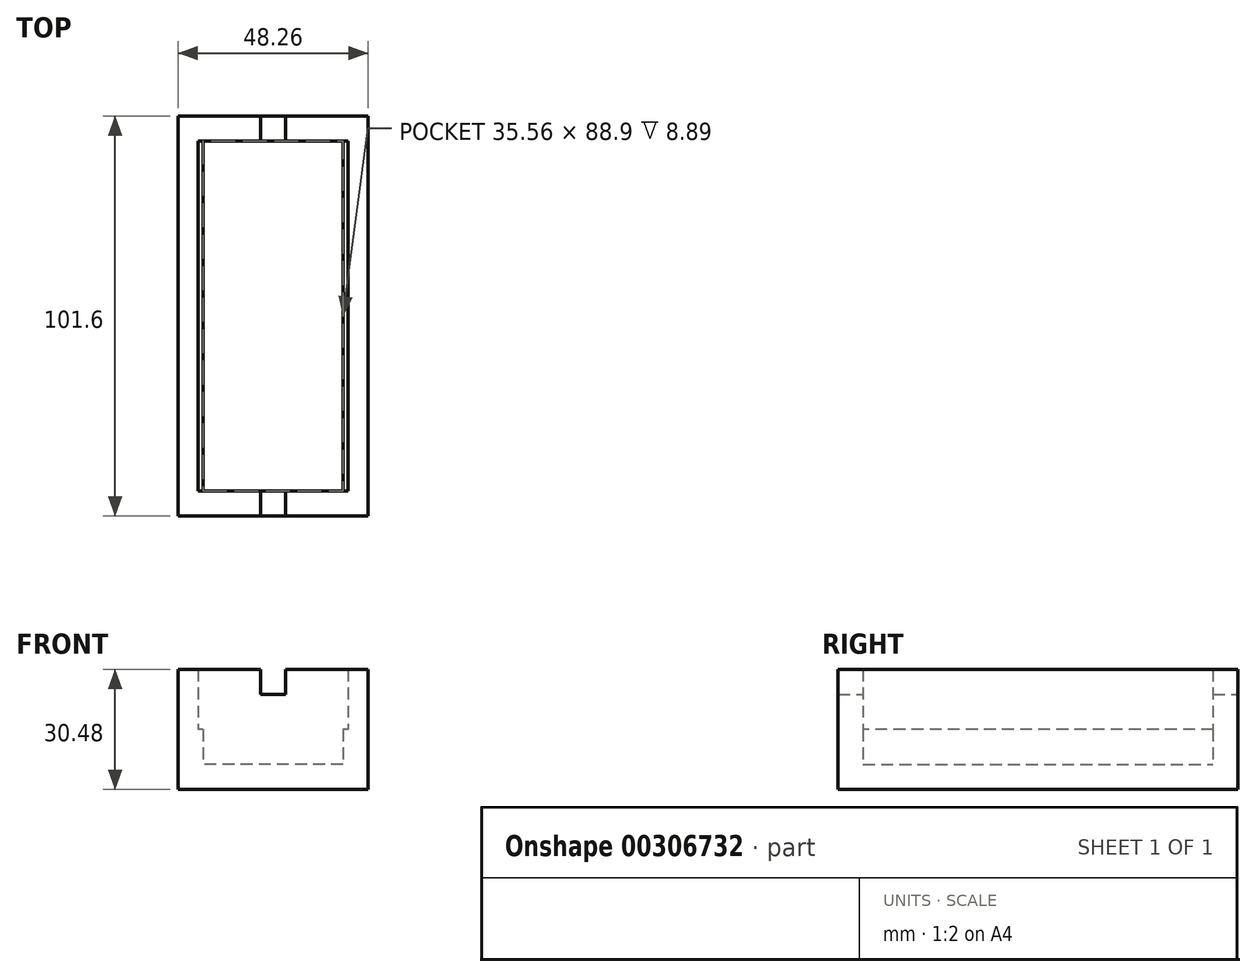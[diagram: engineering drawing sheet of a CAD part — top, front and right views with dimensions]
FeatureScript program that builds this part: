
annotation { "Feature Type Name" : "Feature", "Feature Type Description" : "" }
export const myFeature = defineFeature(function(context is Context, id is Id, definition is map)
    precondition{}
    {
        {
            var Q0;
            Q0=qCreatedBy(makeId("Front.planeOp"),FACE);
            var sketch = newSketch(context, id + "F0", { "sketchPlane" : qUnion([Q0])});
            skLineSegment(sketch, "E0.bottom", {"start": v(24.13, 15.24) * mm, "end": v(-24.13, 15.24) * mm});
            skLineSegment(sketch, "E0.top", {"start": v(24.13, -15.24) * mm, "end": v(-24.13, -15.24) * mm});
            skLineSegment(sketch, "E0.left", {"start": v(24.13, 15.24) * mm, "end": v(24.13, -15.24) * mm});
            skLineSegment(sketch, "E0.right", {"start": v(-24.13, 15.24) * mm, "end": v(-24.13, -15.24) * mm});
            skPoint(sketch, "E0.middle", {"position": v(0, 0) * mm});
            skLineSegment(sketch, "E1.bottom", {"start": v(-19.05, 15.24) * mm, "end": v(19.05, 15.24) * mm});
            skLineSegment(sketch, "E1.top", {"start": v(-19.05, -10.16) * mm, "end": v(19.05, -10.16) * mm});
            skLineSegment(sketch, "E1.left", {"start": v(-19.05, 15.24) * mm, "end": v(-19.05, -10.16) * mm});
            skLineSegment(sketch, "E1.right", {"start": v(19.05, 15.24) * mm, "end": v(19.05, -10.16) * mm});
            skLineSegment(sketch, "E2.bottom", {"start": v(-3.17, 15.24) * mm, "end": v(3.18, 15.24) * mm});
            skLineSegment(sketch, "E3.top", {"start": v(-3.17, 8.87) * mm, "end": v(3.18, 8.87) * mm});
            skLineSegment(sketch, "E3.left", {"start": v(-3.17, 15.24) * mm, "end": v(-3.17, 8.87) * mm});
            skLineSegment(sketch, "E3.right", {"start": v(3.18, 15.24) * mm, "end": v(3.18, 8.87) * mm});
            skSolve(sketch);
        }
        {
            var Q0;
            Q0=makeQuery(id+"F0.imprint","IMPRINT",FACE,{"disambiguationData":[TD([[makeQuery(id+"F0.imprint","IMPRINT",EDGE,{"derivedFrom":sQuery(id+"F0.wireOp",EDGE,"E0.top")}),-1.0]])]});
            extrude(context, id + "F1", {"entities" : qUnion([Q0]), "depth" : 50.8 * mm});
        }
        {
            var Q0;
            Q0=makeQuery(id+"F0.imprint","IMPRINT",FACE,{"disambiguationData":[TD([[makeQuery(id+"F0.imprint","IMPRINT",EDGE,{"derivedFrom":sQuery(id+"F0.wireOp",EDGE,"E1.top")}),1.0]])]});
            extrude(context, id + "F2", {"entities" : qUnion([Q0]), "operationType" : NewBodyOperationType.ADD, "depth" : 50.8 * mm});
        }
        {
            var Q0;
            Q0=makeQuery(id+"F1.opExtrude","SWEPT_BODY",BODY,{"disambiguationData":[OSD([sQuery(id+"F0.wireOp",EDGE,"E0.bottom"),sQuery(id+"F0.wireOp",EDGE,"E0.top"),sQuery(id+"F0.wireOp",EDGE,"E0.left"),sQuery(id+"F0.wireOp",EDGE,"E0.right"),sQuery(id+"F0.wireOp",EDGE,"E1.top"),sQuery(id+"F0.wireOp",EDGE,"E1.left"),sQuery(id+"F0.wireOp",EDGE,"E1.right")])]});
            var Q1;
            Q1=qCreatedBy(makeId("Front.planeOp"),FACE);
            mirror(context, id + "F3", {"operationType" : NewBodyOperationType.ADD, "entities" : qUnion([Q0]), "mirrorPlane" : qUnion([Q1])});
        }
        {
            var Q0;
            Q0=qCreatedBy(makeId("Top.planeOp"),FACE);
            var sketch = newSketch(context, id + "F4", { "sketchPlane" : qUnion([Q0])});
            skLineSegment(sketch, "E4.bottom", {"start": v(19.05, 44.45) * mm, "end": v(-19.05, 44.45) * mm});
            skLineSegment(sketch, "E4.top", {"start": v(19.05, -44.45) * mm, "end": v(-19.05, -44.45) * mm});
            skLineSegment(sketch, "E4.left", {"start": v(19.05, 44.45) * mm, "end": v(19.05, -44.45) * mm});
            skLineSegment(sketch, "E4.right", {"start": v(-19.05, 44.45) * mm, "end": v(-19.05, -44.45) * mm});
            skPoint(sketch, "E4.middle", {"position": v(0, 0) * mm});
            skLineSegment(sketch, "E5.bottom", {"start": v(25.4, 50.8) * mm, "end": v(-25.4, 50.8) * mm});
            skLineSegment(sketch, "E5.top", {"start": v(25.4, -50.8) * mm, "end": v(-25.4, -50.8) * mm});
            skLineSegment(sketch, "E5.left", {"start": v(25.4, 50.8) * mm, "end": v(25.4, -50.8) * mm});
            skLineSegment(sketch, "E5.right", {"start": v(-25.4, 50.8) * mm, "end": v(-25.4, -50.8) * mm});
            skSolve(sketch);
        }
        {
            var Q0;
            {var subQ0=sQuery(id+"F0.wireOp",EDGE,"E1.bottom");var subQ1=sQuery(id+"F0.wireOp",EDGE,"E0.bottom");var subQ2=makeQuery(id+"F2.boolean.opBoolean","MERGE",FACE,{"derivedFrom":[makeQuery(id+"F1.opExtrude","SWEPT_FACE",FACE,{"disambiguationData":[OSD([subQ1]),TDD([makeQuery(id+"F0.imprint","IMPRINT",EDGE,{"disambiguationData":[TD([[makeQuery(id+"F0.imprint","INTERSECT",VERTEX,{"derivedFrom":[subQ1,sQuery(id+"F0.wireOp",EDGE,"E0.left")]}),-1.0]])],"derivedFrom":subQ1})])]}),makeQuery(id+"F1.opExtrude","SWEPT_FACE",FACE,{"disambiguationData":[OSD([subQ1]),TDD([makeQuery(id+"F0.imprint","IMPRINT",EDGE,{"disambiguationData":[TD([[makeQuery(id+"F0.imprint","INTERSECT",VERTEX,{"derivedFrom":[subQ1,sQuery(id+"F0.wireOp",EDGE,"E0.right")]}),1.0]])],"derivedFrom":subQ1})])]}),makeQuery(id+"F2.opExtrude","SWEPT_FACE",FACE,{"disambiguationData":[OSD([subQ0,sQuery(id+"F0.wireOp",EDGE,"E2.bottom")])]})]});Q0=makeQuery(id+"F3.boolean.opBoolean","MERGE",FACE,{"derivedFrom":[subQ2,makeQuery(id+"F3.opPattern","COPY",FACE,{"derivedFrom":subQ2,"instanceName":"1"})]});}
            shell(context, id + "F5", {"entities" : qUnion([Q0]), "thickness" : 6.35 * mm});
        }
        {
            var Q0;
            Q0=makeQuery(id+"F4.imprint","IMPRINT",FACE,{"disambiguationData":[TD([[makeQuery(id+"F4.imprint","IMPRINT",EDGE,{"derivedFrom":sQuery(id+"F4.wireOp",EDGE,"E4.bottom")}),1.0]])]});
            extrude(context, id + "F6", {"entities" : qUnion([Q0]), "operationType" : NewBodyOperationType.REMOVE, "oppositeDirection" : true, "depth" : -31.75 * mm});
        }
    });
